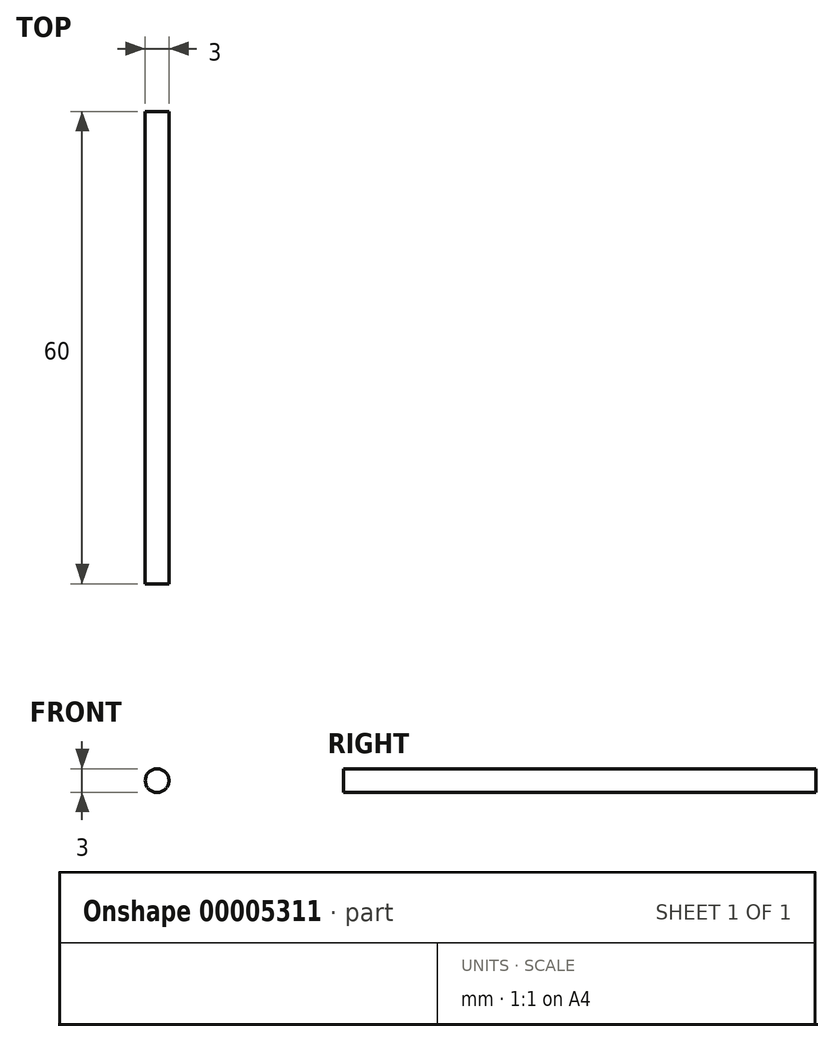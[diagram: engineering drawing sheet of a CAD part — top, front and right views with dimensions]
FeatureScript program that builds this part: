
annotation { "Feature Type Name" : "Feature", "Feature Type Description" : "" }
export const myFeature = defineFeature(function(context is Context, id is Id, definition is map)
    precondition{}
    {
        {
            var Q0;
            Q0=qCreatedBy(makeId("Front.planeOp"),FACE);
            var sketch = newSketch(context, id + "F0", { "sketchPlane" : qUnion([Q0])});
            skCircle(sketch, "E0", {"center": v(0, 0) * mm, "radius": 1.5 * mm});
            skSolve(sketch);
        }
        {
            var Q0;
            Q0=makeQuery(id+"F0.imprint","IMPRINT",FACE,{"disambiguationData":[TD([[makeQuery(id+"F0.imprint","IMPRINT",EDGE,{"derivedFrom":sQuery(id+"F0.wireOp",EDGE,"E0")}),1.0]])]});
            extrude(context, id + "F1", {"entities" : qUnion([Q0]), "depth" : 60 * mm});
        }
    });
